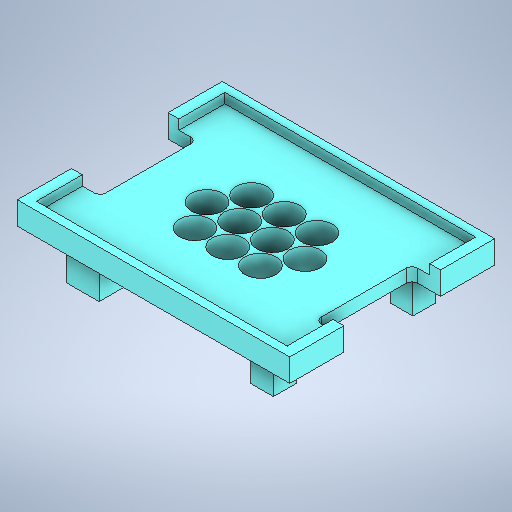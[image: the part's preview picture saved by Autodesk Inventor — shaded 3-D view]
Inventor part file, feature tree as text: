
AUTODESK INVENTOR PART (.ipt)
format: ipt  version: 2025.2 (Build 292293000, 293)  size: 1,046,528 bytes
history: native  units: mm
features: extrude x8, sketch x8, projected_geometry x8
ambient origin geometry x8: Origin, YZ Plane, XZ Plane, XY Plane, X Axis, Y Axis, Z Axis, Center Point
bodies: Solid1 (feature_tree)
feature tree (24):
  extrude  "Extrusion1"  Depth=19.0mm
  sketch  "Sketch4"  dims[d4=19.0mm d6=19.0mm]
  extrude  "Extrusion7"  Depth=19.0mm
  sketch  "Sketch5"  dims[d8=19.0mm d10=19.0mm]
  extrude  "Extrusion8"  Depth=19.0mm
  extrude  "Extrusion6"  Depth=19.0mm
  extrude  "Extrusion9"  Depth=15.0mm TaperAngle=0.0deg
  extrude  "Extrusion11"  Depth=1.0mm
  extrude  "Extrusion12"  Depth=0.5mm
  extrude  "Extrusion14"  Depth=0.5mm
  sketch  "Sketch1"  dims[d0=19.0mm d2=19.0mm]
  projected_geometry  "Projected Loop1"
  sketch  "Sketch6"  dims[d11=19.0mm d13=19.0mm]
  projected_geometry  "Projected Loop4"
  sketch  "Sketch7"  dims[d14=19.0mm]
  projected_geometry  "Projected Loop5"
  projected_geometry  "Projected Loop6"
  sketch  "Sketch10"  dims[d16=20.0mm d17=20.0mm d18=20.0mm d19=20.0mm d20=20.0mm d21=20.0mm d22=20.0mm d23=20.0mm d24=15.0mm d25=0.0mm]
  projected_geometry  "Projected Loop9"
  sketch  "Sketch11"  dims[d53=19.0mm d91=1.0mm]
  projected_geometry  "Projected Loop10"
  projected_geometry  "Projected Loop11"
  sketch  "Sketch13"  dims[d104=153.4mm d123=7.23mm d124=7.23mm d125=7.23mm d126=0.0mm d127=0.0mm d140=7.23mm d144=21.0mm d145=21.0mm d146=21.0mm d147=21.0mm d148=21.0mm d149=21.0mm d150=21.0mm d151=21.0mm d152=21.0mm d153=21.0mm d154=23.0mm d155=23.0mm d156=23.0mm d157=23.0mm d158=23.0mm d159=23.0mm d160=23.0mm d161=23.0mm d162=23.0mm d163=23.0mm d164=115.4mm d165=8.0mm d166=0.0mm d169=5.0mm d170=6.646447mm d171=166.692894mm d172=125.4mm d173=6.0mm d174=8.0mm d175=0.0mm d176=0.0mm d177=0.0mm d178=0.0mm d179=31.75mm d180=7.228mm d181=7.228mm d182=31.75mm d183=31.75mm d184=7.228mm d185=7.228mm d186=31.75mm d209=30.0mm d210=20.0mm d211=20.0mm d212=20.0mm d213=15.0mm d214=15.0mm d215=30.0mm d216=20.0mm d217=14.0mm d218=14.0mm d219=25.0mm d220=0.0mm d221=6.646447mm d222=70.0mm d223=0.0mm d224=30.0mm d225=30.0mm d226=20.0mm d227=20.0mm d231=10.0mm d232=0.0mm d228=0.5mm d229=0.872665mm d230=0.5mm]
  projected_geometry  "Projected Loop13"
